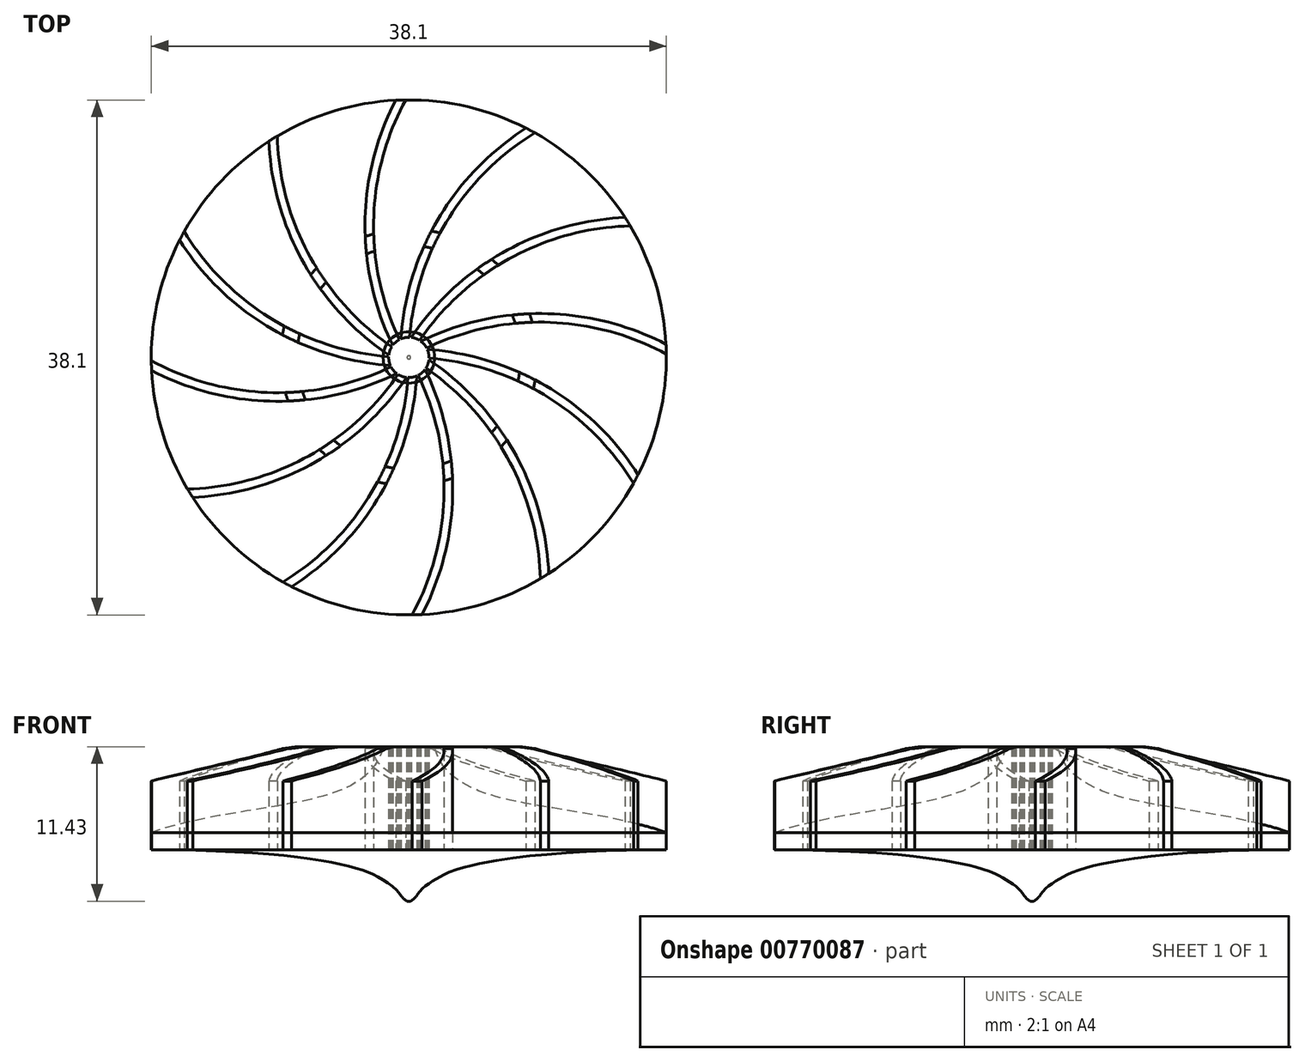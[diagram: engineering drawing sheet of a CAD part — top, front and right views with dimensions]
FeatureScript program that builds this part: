
annotation { "Feature Type Name" : "Feature", "Feature Type Description" : "" }
export const myFeature = defineFeature(function(context is Context, id is Id, definition is map)
    precondition{}
    {
        {
            var Q0;
            Q0=qCreatedBy(makeId("Top.planeOp"),FACE);
            var sketch = newSketch(context, id + "F0", { "sketchPlane" : qUnion([Q0])});
            skCircle(sketch, "E0", {"center": v(0, 0) * mm, "radius": 19.05 * mm});
            skPoint(sketch, "E1", {"position": v(-0.24, 19.05) * mm});
            skPoint(sketch, "E2.1.0", {"position": v(-9.73, 16.38) * mm});
            skPoint(sketch, "E2.2.0", {"position": v(-16.62, 9.32) * mm});
            skPoint(sketch, "E3.0.3.0", {"position": v(-19.05, -0.24) * mm});
            skPoint(sketch, "E3.0.4.0", {"position": v(-16.38, -9.73) * mm});
            skPoint(sketch, "E3.0.5.0", {"position": v(-9.32, -16.62) * mm});
            skPoint(sketch, "E3.0.6.0", {"position": v(0.24, -19.05) * mm});
            skPoint(sketch, "E3.0.7.0", {"position": v(9.73, -16.38) * mm});
            skPoint(sketch, "E3.0.8.0", {"position": v(16.62, -9.32) * mm});
            skPoint(sketch, "E3.0.9.0", {"position": v(19.05, 0.24) * mm});
            skPoint(sketch, "E3.0.10.0", {"position": v(16.38, 9.73) * mm});
            skPoint(sketch, "E3.0.11.0", {"position": v(9.32, 16.62) * mm});
            skArc(sketch, "E4", {"start": v(9.32, 16.62) * mm, "mid": v(2.49, 9.53) * mm, "end": v(0, 0) * mm});
            skArc(sketch, "E5.0", {"start": v(8.67, 16.96) * mm, "mid": v(1.84, 9.67) * mm, "end": v(-0.63, 0) * mm});
            skArc(sketch, "E6.1.0", {"start": v(-0.24, 19.05) * mm, "mid": v(-2.6, 9.5) * mm, "end": v(0, 0) * mm});
            skArc(sketch, "E6.1.1", {"start": v(-0.97, 19.03) * mm, "mid": v(-3.24, 9.3) * mm, "end": v(-0.55, -0.32) * mm});
            skArc(sketch, "E6.2.0", {"start": v(-9.73, 16.38) * mm, "mid": v(-7, 6.92) * mm, "end": v(0, 0) * mm});
            skArc(sketch, "E6.2.1", {"start": v(-10.35, 16) * mm, "mid": v(-7.46, 6.43) * mm, "end": v(-0.32, -0.55) * mm});
            skArc(sketch, "E6.3.0", {"start": v(-16.62, 9.32) * mm, "mid": v(-9.53, 2.49) * mm, "end": v(0, 0) * mm});
            skArc(sketch, "E6.3.1", {"start": v(-16.96, 8.67) * mm, "mid": v(-9.67, 1.84) * mm, "end": v(0, -0.63) * mm});
            skArc(sketch, "E6.4.0", {"start": v(-19.05, -0.24) * mm, "mid": v(-9.5, -2.6) * mm, "end": v(0, 0) * mm});
            skArc(sketch, "E6.4.1", {"start": v(-19.03, -0.97) * mm, "mid": v(-9.3, -3.24) * mm, "end": v(0.32, -0.55) * mm});
            skArc(sketch, "E6.5.0", {"start": v(-16.38, -9.73) * mm, "mid": v(-6.92, -7) * mm, "end": v(0, 0) * mm});
            skArc(sketch, "E6.5.1", {"start": v(-16, -10.35) * mm, "mid": v(-6.43, -7.46) * mm, "end": v(0.55, -0.32) * mm});
            skArc(sketch, "E6.6.0", {"start": v(-9.32, -16.62) * mm, "mid": v(-2.49, -9.53) * mm, "end": v(0, 0) * mm});
            skArc(sketch, "E6.6.1", {"start": v(-8.67, -16.96) * mm, "mid": v(-1.84, -9.67) * mm, "end": v(0.63, 0) * mm});
            skArc(sketch, "E6.7.0", {"start": v(0.24, -19.05) * mm, "mid": v(2.6, -9.5) * mm, "end": v(0, 0) * mm});
            skArc(sketch, "E6.7.1", {"start": v(0.97, -19.03) * mm, "mid": v(3.24, -9.3) * mm, "end": v(0.55, 0.32) * mm});
            skArc(sketch, "E6.8.0", {"start": v(9.73, -16.38) * mm, "mid": v(7, -6.92) * mm, "end": v(0, 0) * mm});
            skArc(sketch, "E6.8.1", {"start": v(10.35, -16) * mm, "mid": v(7.46, -6.43) * mm, "end": v(0.32, 0.55) * mm});
            skArc(sketch, "E6.9.0", {"start": v(16.62, -9.32) * mm, "mid": v(9.53, -2.49) * mm, "end": v(0, 0) * mm});
            skArc(sketch, "E6.9.1", {"start": v(16.96, -8.67) * mm, "mid": v(9.67, -1.84) * mm, "end": v(0, 0.63) * mm});
            skArc(sketch, "E6.10.0", {"start": v(19.05, 0.24) * mm, "mid": v(9.5, 2.6) * mm, "end": v(0, 0) * mm});
            skArc(sketch, "E6.10.1", {"start": v(19.03, 0.97) * mm, "mid": v(9.3, 3.24) * mm, "end": v(-0.32, 0.55) * mm});
            skArc(sketch, "E6.11.0", {"start": v(16.38, 9.73) * mm, "mid": v(6.92, 7) * mm, "end": v(0, 0) * mm});
            skArc(sketch, "E6.11.1", {"start": v(16, 10.35) * mm, "mid": v(6.43, 7.46) * mm, "end": v(-0.55, 0.32) * mm});
            skCircle(sketch, "E7", {"center": v(0, 0) * mm, "radius": 1.5 * mm});
            skSolve(sketch);
        }
        {
            var Q0;
            Q0=qCreatedBy(makeId("Top.planeOp"),FACE);
            var sketch = newSketch(context, id + "F1", { "sketchPlane" : qUnion([Q0])});
            skCircle(sketch, "E8", {"center": v(0, 0) * mm, "radius": 19.05 * mm});
            skSolve(sketch);
        }
        {
            var Q0;
            Q0 = qSketchRegion(id + "F1", true);
            extrude(context, id + "F2", {"entities" : qUnion([Q0]), "depth" : 6.35 * mm, "offsetDistance" : 25.4 * mm, "hasSecondDirection" : true, "secondDirectionOppositeDirection" : true, "secondDirectionDepth" : 1.27 * mm});
        }
        {
            var Q0;
            Q0=qCreatedBy(makeId("Front.planeOp"),FACE);
            var sketch = newSketch(context, id + "F3", { "sketchPlane" : qUnion([Q0])});
            skLineSegment(sketch, "E9.bottom", {"start": v(19.05, 6.35) * mm, "end": v(-19.05, 6.35) * mm});
            skLineSegment(sketch, "E9.left", {"start": v(19.05, 6.35) * mm, "end": v(19.05, -5.08) * mm});
            skLineSegment(sketch, "E9.right", {"start": v(-19.05, 6.35) * mm, "end": v(-19.05, -5.08) * mm});
            skPoint(sketch, "E9.middle", {"position": v(0, 0) * mm});
            skLineSegment(sketch, "E10", {"start": v(-19.05, -5.08) * mm, "end": v(19.05, -5.08) * mm});
            skLineSegment(sketch, "E11", {"start": v(-19.05, 0) * mm, "end": v(19.05, 0) * mm, "construction": true});
            skLineSegment(sketch, "E12", {"start": v(0, -5.08) * mm, "end": v(0, 6.35) * mm, "construction": true});
            skPoint(sketch, "E13", {"position": v(1.9, 6.35) * mm});
            skPoint(sketch, "E14", {"position": v(19.05, 1.27) * mm});
            skFitSpline(sketch, "E15", {"points": [v(1.9, 6.35) * mm, v(5.08, 3.11) * mm, v(19.05, 0) * mm, v(28.85, -6.98) * mm], "startDerivative": vector(3.87, -17.8) * mm, "endDerivative": vector(21.57, -22.67) * mm});
            skLineSegment(sketch, "E16", {"start": v(1.9, 6.35) * mm, "end": v(19.05, 6.35) * mm});
            skFitSpline(sketch, "E17", {"points": [v(19.05, -1.28) * mm, v(4.25, -2.54) * mm, v(2.03, -3.42) * mm, v(0.5, -4.83) * mm], "startDerivative": vector(-41.63, 0) * mm, "endDerivative": vector(-3.76, -8.36) * mm});
            skArc(sketch, "E18", {"start": v(0.13, -5.08) * mm, "mid": v(0.4, -4.87) * mm, "end": v(0.64, -4.6) * mm});
            skLineSegment(sketch, "E19", {"start": v(0, -5.08) * mm, "end": v(0, -1.28) * mm});
            skLineSegment(sketch, "E20", {"start": v(0, -1.28) * mm, "end": v(19.05, -1.28) * mm});
            skSolve(sketch);
        }
        {
            var Q0;
            {var subQ0=sQuery(id+"F3.wireOp",EDGE,"E15");Q0=makeQuery(id+"F3.imprint","IMPRINT",FACE,{"disambiguationData":[TD([[makeQuery(id+"F3.imprint","IMPRINT",EDGE,{"derivedFrom":subQ0}),1.0]])]});}
            var Q1;
            Q1=sQuery(id+"F3.wireOp",EDGE,"E12");
            revolve(context, id + "F4", {"operationType" : NewBodyOperationType.REMOVE, "surfaceOperationType" : NewSurfaceOperationType.NEW, "entities" : qUnion([Q0]), "axis" : qUnion([Q1]), "revolveType" : RevolveType.FULL});
        }
        {
            var Q0;
            {var subQ0=sQuery(id+"F0.wireOp",EDGE,"E6.4.0");var subQ1=sQuery(id+"F0.wireOp",EDGE,"E0");var subQ2=makeQuery(id+"F0.imprint","INTERSECT",VERTEX,{"derivedFrom":[subQ1,subQ0]});Q0=makeQuery(id+"F0.imprint","IMPRINT",FACE,{"disambiguationData":[TD([[makeQuery(id+"F0.imprint","IMPRINT",EDGE,{"disambiguationData":[TD([[subQ2,-1.0]])],"derivedFrom":subQ1}),1.0]])]});}
            var Q1;
            {var subQ0=sQuery(id+"F0.wireOp",EDGE,"E6.9.0");var subQ1=sQuery(id+"F0.wireOp",EDGE,"E0");var subQ2=makeQuery(id+"F0.imprint","INTERSECT",VERTEX,{"derivedFrom":[subQ1,subQ0]});Q1=makeQuery(id+"F0.imprint","IMPRINT",FACE,{"disambiguationData":[TD([[makeQuery(id+"F0.imprint","IMPRINT",EDGE,{"disambiguationData":[TD([[subQ2,-1.0]])],"derivedFrom":subQ1}),1.0]])]});}
            var Q2;
            {var subQ0=sQuery(id+"F0.wireOp",EDGE,"E6.6.0");var subQ1=sQuery(id+"F0.wireOp",EDGE,"E0");var subQ2=makeQuery(id+"F0.imprint","INTERSECT",VERTEX,{"derivedFrom":[subQ1,subQ0]});Q2=makeQuery(id+"F0.imprint","IMPRINT",FACE,{"disambiguationData":[TD([[makeQuery(id+"F0.imprint","IMPRINT",EDGE,{"disambiguationData":[TD([[subQ2,-1.0]])],"derivedFrom":subQ1}),1.0]])]});}
            var Q3;
            {var subQ0=sQuery(id+"F0.wireOp",EDGE,"E6.10.0");var subQ1=sQuery(id+"F0.wireOp",EDGE,"E0");var subQ2=makeQuery(id+"F0.imprint","INTERSECT",VERTEX,{"derivedFrom":[subQ1,subQ0]});Q3=makeQuery(id+"F0.imprint","IMPRINT",FACE,{"disambiguationData":[TD([[makeQuery(id+"F0.imprint","IMPRINT",EDGE,{"disambiguationData":[TD([[subQ2,-1.0]])],"derivedFrom":subQ1}),1.0]])]});}
            var Q4;
            {var subQ0=sQuery(id+"F0.wireOp",EDGE,"E6.3.0");var subQ1=sQuery(id+"F0.wireOp",EDGE,"E0");var subQ2=makeQuery(id+"F0.imprint","INTERSECT",VERTEX,{"derivedFrom":[subQ1,subQ0]});Q4=makeQuery(id+"F0.imprint","IMPRINT",FACE,{"disambiguationData":[TD([[makeQuery(id+"F0.imprint","IMPRINT",EDGE,{"disambiguationData":[TD([[subQ2,-1.0]])],"derivedFrom":subQ1}),1.0]])]});}
            var Q5;
            {var subQ0=sQuery(id+"F0.wireOp",EDGE,"E6.8.0");var subQ1=sQuery(id+"F0.wireOp",EDGE,"E0");var subQ2=makeQuery(id+"F0.imprint","INTERSECT",VERTEX,{"derivedFrom":[subQ1,subQ0]});Q5=makeQuery(id+"F0.imprint","IMPRINT",FACE,{"disambiguationData":[TD([[makeQuery(id+"F0.imprint","IMPRINT",EDGE,{"disambiguationData":[TD([[subQ2,-1.0]])],"derivedFrom":subQ1}),1.0]])]});}
            var Q6;
            {var subQ0=sQuery(id+"F0.wireOp",EDGE,"E6.7.0");var subQ1=sQuery(id+"F0.wireOp",EDGE,"E0");var subQ2=makeQuery(id+"F0.imprint","INTERSECT",VERTEX,{"derivedFrom":[subQ1,subQ0]});Q6=makeQuery(id+"F0.imprint","IMPRINT",FACE,{"disambiguationData":[TD([[makeQuery(id+"F0.imprint","IMPRINT",EDGE,{"disambiguationData":[TD([[subQ2,-1.0]])],"derivedFrom":subQ1}),1.0]])]});}
            var Q7;
            {var subQ0=sQuery(id+"F0.wireOp",EDGE,"E6.11.0");var subQ1=sQuery(id+"F0.wireOp",EDGE,"E0");var subQ2=makeQuery(id+"F0.imprint","INTERSECT",VERTEX,{"derivedFrom":[subQ1,subQ0]});Q7=makeQuery(id+"F0.imprint","IMPRINT",FACE,{"disambiguationData":[TD([[makeQuery(id+"F0.imprint","IMPRINT",EDGE,{"disambiguationData":[TD([[subQ2,-1.0]])],"derivedFrom":subQ1}),1.0]])]});}
            var Q8;
            {var subQ0=sQuery(id+"F0.wireOp",EDGE,"E6.1.0");var subQ1=sQuery(id+"F0.wireOp",EDGE,"E0");var subQ2=makeQuery(id+"F0.imprint","INTERSECT",VERTEX,{"derivedFrom":[subQ1,subQ0]});Q8=makeQuery(id+"F0.imprint","IMPRINT",FACE,{"disambiguationData":[TD([[makeQuery(id+"F0.imprint","IMPRINT",EDGE,{"disambiguationData":[TD([[subQ2,-1.0]])],"derivedFrom":subQ1}),1.0]])]});}
            var Q9;
            {var subQ0=sQuery(id+"F0.wireOp",EDGE,"E6.5.0");var subQ1=sQuery(id+"F0.wireOp",EDGE,"E0");var subQ2=makeQuery(id+"F0.imprint","INTERSECT",VERTEX,{"derivedFrom":[subQ1,subQ0]});Q9=makeQuery(id+"F0.imprint","IMPRINT",FACE,{"disambiguationData":[TD([[makeQuery(id+"F0.imprint","IMPRINT",EDGE,{"disambiguationData":[TD([[subQ2,-1.0]])],"derivedFrom":subQ1}),1.0]])]});}
            var Q10;
            {var subQ0=sQuery(id+"F0.wireOp",EDGE,"E4");var subQ1=sQuery(id+"F0.wireOp",EDGE,"E0");var subQ2=makeQuery(id+"F0.imprint","INTERSECT",VERTEX,{"derivedFrom":[subQ1,subQ0]});Q10=makeQuery(id+"F0.imprint","IMPRINT",FACE,{"disambiguationData":[TD([[makeQuery(id+"F0.imprint","IMPRINT",EDGE,{"disambiguationData":[TD([[subQ2,-1.0]])],"derivedFrom":subQ1}),1.0]])]});}
            var Q11;
            {var subQ0=sQuery(id+"F0.wireOp",EDGE,"E6.2.0");var subQ1=sQuery(id+"F0.wireOp",EDGE,"E0");var subQ2=makeQuery(id+"F0.imprint","INTERSECT",VERTEX,{"derivedFrom":[subQ1,subQ0]});Q11=makeQuery(id+"F0.imprint","IMPRINT",FACE,{"disambiguationData":[TD([[makeQuery(id+"F0.imprint","IMPRINT",EDGE,{"disambiguationData":[TD([[subQ2,-1.0]])],"derivedFrom":subQ1}),1.0]])]});}
            extrude(context, id + "F5", {"entities" : qUnion([Q0, Q1, Q2, Q3, Q4, Q5, Q6, Q7, Q8, Q9, Q10, Q11]), "depth" : 6.35 * mm, "offsetDistance" : 25.4 * mm, "hasSecondDirection" : true, "secondDirectionOppositeDirection" : true, "secondDirectionDepth" : 1.27 * mm});
        }
        {
            var Q0;
            {var subQ0=sQuery(id+"F0.wireOp",EDGE,"E0");Q0=makeQuery(id+"F5.opExtrude","CAP_EDGE",EDGE,{"disambiguationData":[OSD([subQ0]),TDD([makeQuery(id+"F0.imprint","IMPRINT",EDGE,{"disambiguationData":[TD([[makeQuery(id+"F0.imprint","INTERSECT",VERTEX,{"derivedFrom":[subQ0,sQuery(id+"F0.wireOp",EDGE,"E6.8.0")]}),-1.0]])],"derivedFrom":subQ0})])],"isStart":false});}
            var Q1;
            {var subQ0=sQuery(id+"F0.wireOp",EDGE,"E0");Q1=makeQuery(id+"F5.opExtrude","CAP_EDGE",EDGE,{"disambiguationData":[OSD([subQ0]),TDD([makeQuery(id+"F0.imprint","IMPRINT",EDGE,{"disambiguationData":[TD([[makeQuery(id+"F0.imprint","INTERSECT",VERTEX,{"derivedFrom":[subQ0,sQuery(id+"F0.wireOp",EDGE,"E6.7.0")]}),-1.0]])],"derivedFrom":subQ0})])],"isStart":false});}
            var Q2;
            {var subQ0=sQuery(id+"F0.wireOp",EDGE,"E0");Q2=makeQuery(id+"F5.opExtrude","CAP_EDGE",EDGE,{"disambiguationData":[OSD([subQ0]),TDD([makeQuery(id+"F0.imprint","IMPRINT",EDGE,{"disambiguationData":[TD([[makeQuery(id+"F0.imprint","INTERSECT",VERTEX,{"derivedFrom":[subQ0,sQuery(id+"F0.wireOp",EDGE,"E6.6.0")]}),-1.0]])],"derivedFrom":subQ0})])],"isStart":false});}
            var Q3;
            {var subQ0=sQuery(id+"F0.wireOp",EDGE,"E0");Q3=makeQuery(id+"F5.opExtrude","CAP_EDGE",EDGE,{"disambiguationData":[OSD([subQ0]),TDD([makeQuery(id+"F0.imprint","IMPRINT",EDGE,{"disambiguationData":[TD([[makeQuery(id+"F0.imprint","INTERSECT",VERTEX,{"derivedFrom":[subQ0,sQuery(id+"F0.wireOp",EDGE,"E6.5.0")]}),-1.0]])],"derivedFrom":subQ0})])],"isStart":false});}
            var Q4;
            {var subQ0=sQuery(id+"F0.wireOp",EDGE,"E0");Q4=makeQuery(id+"F5.opExtrude","CAP_EDGE",EDGE,{"disambiguationData":[OSD([subQ0]),TDD([makeQuery(id+"F0.imprint","IMPRINT",EDGE,{"disambiguationData":[TD([[makeQuery(id+"F0.imprint","INTERSECT",VERTEX,{"derivedFrom":[subQ0,sQuery(id+"F0.wireOp",EDGE,"E6.4.0")]}),-1.0]])],"derivedFrom":subQ0})])],"isStart":false});}
            var Q5;
            {var subQ0=sQuery(id+"F0.wireOp",EDGE,"E0");Q5=makeQuery(id+"F5.opExtrude","CAP_EDGE",EDGE,{"disambiguationData":[OSD([subQ0]),TDD([makeQuery(id+"F0.imprint","IMPRINT",EDGE,{"disambiguationData":[TD([[makeQuery(id+"F0.imprint","INTERSECT",VERTEX,{"derivedFrom":[subQ0,sQuery(id+"F0.wireOp",EDGE,"E6.3.0")]}),-1.0]])],"derivedFrom":subQ0})])],"isStart":false});}
            var Q6;
            {var subQ0=sQuery(id+"F0.wireOp",EDGE,"E0");Q6=makeQuery(id+"F5.opExtrude","CAP_EDGE",EDGE,{"disambiguationData":[OSD([subQ0]),TDD([makeQuery(id+"F0.imprint","IMPRINT",EDGE,{"disambiguationData":[TD([[makeQuery(id+"F0.imprint","INTERSECT",VERTEX,{"derivedFrom":[subQ0,sQuery(id+"F0.wireOp",EDGE,"E6.2.0")]}),-1.0]])],"derivedFrom":subQ0})])],"isStart":false});}
            var Q7;
            {var subQ0=sQuery(id+"F0.wireOp",EDGE,"E0");Q7=makeQuery(id+"F5.opExtrude","CAP_EDGE",EDGE,{"disambiguationData":[OSD([subQ0]),TDD([makeQuery(id+"F0.imprint","IMPRINT",EDGE,{"disambiguationData":[TD([[makeQuery(id+"F0.imprint","INTERSECT",VERTEX,{"derivedFrom":[subQ0,sQuery(id+"F0.wireOp",EDGE,"E6.1.0")]}),-1.0]])],"derivedFrom":subQ0})])],"isStart":false});}
            var Q8;
            {var subQ0=sQuery(id+"F0.wireOp",EDGE,"E0");Q8=makeQuery(id+"F5.opExtrude","CAP_EDGE",EDGE,{"disambiguationData":[OSD([subQ0]),TDD([makeQuery(id+"F0.imprint","IMPRINT",EDGE,{"disambiguationData":[TD([[makeQuery(id+"F0.imprint","INTERSECT",VERTEX,{"derivedFrom":[subQ0,sQuery(id+"F0.wireOp",EDGE,"E4")]}),-1.0]])],"derivedFrom":subQ0})])],"isStart":false});}
            var Q9;
            {var subQ0=sQuery(id+"F0.wireOp",EDGE,"E0");Q9=makeQuery(id+"F5.opExtrude","CAP_EDGE",EDGE,{"disambiguationData":[OSD([subQ0]),TDD([makeQuery(id+"F0.imprint","IMPRINT",EDGE,{"disambiguationData":[TD([[makeQuery(id+"F0.imprint","INTERSECT",VERTEX,{"derivedFrom":[subQ0,sQuery(id+"F0.wireOp",EDGE,"E6.11.0")]}),-1.0]])],"derivedFrom":subQ0})])],"isStart":false});}
            var Q10;
            {var subQ0=sQuery(id+"F0.wireOp",EDGE,"E0");Q10=makeQuery(id+"F5.opExtrude","CAP_EDGE",EDGE,{"disambiguationData":[OSD([subQ0]),TDD([makeQuery(id+"F0.imprint","IMPRINT",EDGE,{"disambiguationData":[TD([[makeQuery(id+"F0.imprint","INTERSECT",VERTEX,{"derivedFrom":[subQ0,sQuery(id+"F0.wireOp",EDGE,"E6.10.0")]}),-1.0]])],"derivedFrom":subQ0})])],"isStart":false});}
            var Q11;
            {var subQ0=sQuery(id+"F0.wireOp",EDGE,"E0");Q11=makeQuery(id+"F5.opExtrude","CAP_EDGE",EDGE,{"disambiguationData":[OSD([subQ0]),TDD([makeQuery(id+"F0.imprint","IMPRINT",EDGE,{"disambiguationData":[TD([[makeQuery(id+"F0.imprint","INTERSECT",VERTEX,{"derivedFrom":[subQ0,sQuery(id+"F0.wireOp",EDGE,"E6.9.0")]}),-1.0]])],"derivedFrom":subQ0})])],"isStart":false});}
            chamfer(context, id + "F6", {"entities" : qUnion([Q0, Q1, Q2, Q3, Q4, Q5, Q6, Q7, Q8, Q9, Q10, Q11]), "chamferType" : ChamferType.TWO_OFFSETS, "width1" : 10.16 * mm, "oppositeDirection" : false, "width2" : 2.54 * mm, "tangentPropagation" : true});
        }
        {
            var Q0;
            {var subQ0=sQuery(id+"F0.wireOp",EDGE,"E6.8.1");var subQ1=sQuery(id+"F0.wireOp",EDGE,"E6.8.0");var subQ2=sQuery(id+"F0.wireOp",EDGE,"E0");Q0=makeQuery(id+"F6.opChamfer","BLEND_EDGE",EDGE,{"blendedFrom":[makeQuery(id+"F5.opExtrude","CAP_EDGE",EDGE,{"disambiguationData":[OSD([subQ2]),TDD([makeQuery(id+"F0.imprint","IMPRINT",EDGE,{"disambiguationData":[TD([[makeQuery(id+"F0.imprint","INTERSECT",VERTEX,{"derivedFrom":[subQ2,subQ1]}),-1.0]])],"derivedFrom":subQ2})])],"isStart":false}),makeQuery(id+"F5.opExtrude","CAP_FACE",FACE,{"disambiguationData":[OSD([subQ2,subQ1,subQ0,sQuery(id+"F0.wireOp",EDGE,"E7")])],"isStart":false})],"blendedInto":[makeQuery(id+"F5.opExtrude","CAP_FACE",FACE,{"disambiguationData":[OSD([subQ2,subQ1,subQ0,sQuery(id+"F0.wireOp",EDGE,"E7")])],"isStart":false})]});}
            var Q1;
            {var subQ0=sQuery(id+"F0.wireOp",EDGE,"E6.7.1");var subQ1=sQuery(id+"F0.wireOp",EDGE,"E6.7.0");var subQ2=sQuery(id+"F0.wireOp",EDGE,"E0");Q1=makeQuery(id+"F6.opChamfer","BLEND_EDGE",EDGE,{"blendedFrom":[makeQuery(id+"F5.opExtrude","CAP_EDGE",EDGE,{"disambiguationData":[OSD([subQ2]),TDD([makeQuery(id+"F0.imprint","IMPRINT",EDGE,{"disambiguationData":[TD([[makeQuery(id+"F0.imprint","INTERSECT",VERTEX,{"derivedFrom":[subQ2,subQ1]}),-1.0]])],"derivedFrom":subQ2})])],"isStart":false}),makeQuery(id+"F5.opExtrude","CAP_FACE",FACE,{"disambiguationData":[OSD([subQ2,subQ1,subQ0,sQuery(id+"F0.wireOp",EDGE,"E7")])],"isStart":false})],"blendedInto":[makeQuery(id+"F5.opExtrude","CAP_FACE",FACE,{"disambiguationData":[OSD([subQ2,subQ1,subQ0,sQuery(id+"F0.wireOp",EDGE,"E7")])],"isStart":false})]});}
            var Q2;
            {var subQ0=sQuery(id+"F0.wireOp",EDGE,"E6.9.1");var subQ1=sQuery(id+"F0.wireOp",EDGE,"E6.9.0");var subQ2=sQuery(id+"F0.wireOp",EDGE,"E0");Q2=makeQuery(id+"F6.opChamfer","BLEND_EDGE",EDGE,{"blendedFrom":[makeQuery(id+"F5.opExtrude","CAP_EDGE",EDGE,{"disambiguationData":[OSD([subQ2]),TDD([makeQuery(id+"F0.imprint","IMPRINT",EDGE,{"disambiguationData":[TD([[makeQuery(id+"F0.imprint","INTERSECT",VERTEX,{"derivedFrom":[subQ2,subQ1]}),-1.0]])],"derivedFrom":subQ2})])],"isStart":false}),makeQuery(id+"F5.opExtrude","CAP_FACE",FACE,{"disambiguationData":[OSD([subQ2,subQ1,subQ0,sQuery(id+"F0.wireOp",EDGE,"E7")])],"isStart":false})],"blendedInto":[makeQuery(id+"F5.opExtrude","CAP_FACE",FACE,{"disambiguationData":[OSD([subQ2,subQ1,subQ0,sQuery(id+"F0.wireOp",EDGE,"E7")])],"isStart":false})]});}
            var Q3;
            {var subQ0=sQuery(id+"F0.wireOp",EDGE,"E6.10.1");var subQ1=sQuery(id+"F0.wireOp",EDGE,"E6.10.0");var subQ2=sQuery(id+"F0.wireOp",EDGE,"E0");Q3=makeQuery(id+"F6.opChamfer","BLEND_EDGE",EDGE,{"blendedFrom":[makeQuery(id+"F5.opExtrude","CAP_EDGE",EDGE,{"disambiguationData":[OSD([subQ2]),TDD([makeQuery(id+"F0.imprint","IMPRINT",EDGE,{"disambiguationData":[TD([[makeQuery(id+"F0.imprint","INTERSECT",VERTEX,{"derivedFrom":[subQ2,subQ1]}),-1.0]])],"derivedFrom":subQ2})])],"isStart":false}),makeQuery(id+"F5.opExtrude","CAP_FACE",FACE,{"disambiguationData":[OSD([subQ2,subQ1,subQ0,sQuery(id+"F0.wireOp",EDGE,"E7")])],"isStart":false})],"blendedInto":[makeQuery(id+"F5.opExtrude","CAP_FACE",FACE,{"disambiguationData":[OSD([subQ2,subQ1,subQ0,sQuery(id+"F0.wireOp",EDGE,"E7")])],"isStart":false})]});}
            var Q4;
            {var subQ0=sQuery(id+"F0.wireOp",EDGE,"E6.11.1");var subQ1=sQuery(id+"F0.wireOp",EDGE,"E6.11.0");var subQ2=sQuery(id+"F0.wireOp",EDGE,"E0");Q4=makeQuery(id+"F6.opChamfer","BLEND_EDGE",EDGE,{"blendedFrom":[makeQuery(id+"F5.opExtrude","CAP_EDGE",EDGE,{"disambiguationData":[OSD([subQ2]),TDD([makeQuery(id+"F0.imprint","IMPRINT",EDGE,{"disambiguationData":[TD([[makeQuery(id+"F0.imprint","INTERSECT",VERTEX,{"derivedFrom":[subQ2,subQ1]}),-1.0]])],"derivedFrom":subQ2})])],"isStart":false}),makeQuery(id+"F5.opExtrude","CAP_FACE",FACE,{"disambiguationData":[OSD([subQ2,subQ1,subQ0,sQuery(id+"F0.wireOp",EDGE,"E7")])],"isStart":false})],"blendedInto":[makeQuery(id+"F5.opExtrude","CAP_FACE",FACE,{"disambiguationData":[OSD([subQ2,subQ1,subQ0,sQuery(id+"F0.wireOp",EDGE,"E7")])],"isStart":false})]});}
            var Q5;
            {var subQ0=sQuery(id+"F0.wireOp",EDGE,"E5.0");var subQ1=sQuery(id+"F0.wireOp",EDGE,"E4");var subQ2=sQuery(id+"F0.wireOp",EDGE,"E0");Q5=makeQuery(id+"F6.opChamfer","BLEND_EDGE",EDGE,{"blendedFrom":[makeQuery(id+"F5.opExtrude","CAP_EDGE",EDGE,{"disambiguationData":[OSD([subQ2]),TDD([makeQuery(id+"F0.imprint","IMPRINT",EDGE,{"disambiguationData":[TD([[makeQuery(id+"F0.imprint","INTERSECT",VERTEX,{"derivedFrom":[subQ2,subQ1]}),-1.0]])],"derivedFrom":subQ2})])],"isStart":false}),makeQuery(id+"F5.opExtrude","CAP_FACE",FACE,{"disambiguationData":[OSD([subQ2,subQ1,subQ0,sQuery(id+"F0.wireOp",EDGE,"E7")])],"isStart":false})],"blendedInto":[makeQuery(id+"F5.opExtrude","CAP_FACE",FACE,{"disambiguationData":[OSD([subQ2,subQ1,subQ0,sQuery(id+"F0.wireOp",EDGE,"E7")])],"isStart":false})]});}
            var Q6;
            {var subQ0=sQuery(id+"F0.wireOp",EDGE,"E6.1.1");var subQ1=sQuery(id+"F0.wireOp",EDGE,"E6.1.0");var subQ2=sQuery(id+"F0.wireOp",EDGE,"E0");Q6=makeQuery(id+"F6.opChamfer","BLEND_EDGE",EDGE,{"blendedFrom":[makeQuery(id+"F5.opExtrude","CAP_EDGE",EDGE,{"disambiguationData":[OSD([subQ2]),TDD([makeQuery(id+"F0.imprint","IMPRINT",EDGE,{"disambiguationData":[TD([[makeQuery(id+"F0.imprint","INTERSECT",VERTEX,{"derivedFrom":[subQ2,subQ1]}),-1.0]])],"derivedFrom":subQ2})])],"isStart":false}),makeQuery(id+"F5.opExtrude","CAP_FACE",FACE,{"disambiguationData":[OSD([subQ2,subQ1,subQ0,sQuery(id+"F0.wireOp",EDGE,"E7")])],"isStart":false})],"blendedInto":[makeQuery(id+"F5.opExtrude","CAP_FACE",FACE,{"disambiguationData":[OSD([subQ2,subQ1,subQ0,sQuery(id+"F0.wireOp",EDGE,"E7")])],"isStart":false})]});}
            var Q7;
            {var subQ0=sQuery(id+"F0.wireOp",EDGE,"E6.2.1");var subQ1=sQuery(id+"F0.wireOp",EDGE,"E6.2.0");var subQ2=sQuery(id+"F0.wireOp",EDGE,"E0");Q7=makeQuery(id+"F6.opChamfer","BLEND_EDGE",EDGE,{"blendedFrom":[makeQuery(id+"F5.opExtrude","CAP_EDGE",EDGE,{"disambiguationData":[OSD([subQ2]),TDD([makeQuery(id+"F0.imprint","IMPRINT",EDGE,{"disambiguationData":[TD([[makeQuery(id+"F0.imprint","INTERSECT",VERTEX,{"derivedFrom":[subQ2,subQ1]}),-1.0]])],"derivedFrom":subQ2})])],"isStart":false}),makeQuery(id+"F5.opExtrude","CAP_FACE",FACE,{"disambiguationData":[OSD([subQ2,subQ1,subQ0,sQuery(id+"F0.wireOp",EDGE,"E7")])],"isStart":false})],"blendedInto":[makeQuery(id+"F5.opExtrude","CAP_FACE",FACE,{"disambiguationData":[OSD([subQ2,subQ1,subQ0,sQuery(id+"F0.wireOp",EDGE,"E7")])],"isStart":false})]});}
            var Q8;
            {var subQ0=sQuery(id+"F0.wireOp",EDGE,"E6.3.1");var subQ1=sQuery(id+"F0.wireOp",EDGE,"E6.3.0");var subQ2=sQuery(id+"F0.wireOp",EDGE,"E0");Q8=makeQuery(id+"F6.opChamfer","BLEND_EDGE",EDGE,{"blendedFrom":[makeQuery(id+"F5.opExtrude","CAP_EDGE",EDGE,{"disambiguationData":[OSD([subQ2]),TDD([makeQuery(id+"F0.imprint","IMPRINT",EDGE,{"disambiguationData":[TD([[makeQuery(id+"F0.imprint","INTERSECT",VERTEX,{"derivedFrom":[subQ2,subQ1]}),-1.0]])],"derivedFrom":subQ2})])],"isStart":false}),makeQuery(id+"F5.opExtrude","CAP_FACE",FACE,{"disambiguationData":[OSD([subQ2,subQ1,subQ0,sQuery(id+"F0.wireOp",EDGE,"E7")])],"isStart":false})],"blendedInto":[makeQuery(id+"F5.opExtrude","CAP_FACE",FACE,{"disambiguationData":[OSD([subQ2,subQ1,subQ0,sQuery(id+"F0.wireOp",EDGE,"E7")])],"isStart":false})]});}
            var Q9;
            {var subQ0=sQuery(id+"F0.wireOp",EDGE,"E6.4.1");var subQ1=sQuery(id+"F0.wireOp",EDGE,"E6.4.0");var subQ2=sQuery(id+"F0.wireOp",EDGE,"E0");Q9=makeQuery(id+"F6.opChamfer","BLEND_EDGE",EDGE,{"blendedFrom":[makeQuery(id+"F5.opExtrude","CAP_EDGE",EDGE,{"disambiguationData":[OSD([subQ2]),TDD([makeQuery(id+"F0.imprint","IMPRINT",EDGE,{"disambiguationData":[TD([[makeQuery(id+"F0.imprint","INTERSECT",VERTEX,{"derivedFrom":[subQ2,subQ1]}),-1.0]])],"derivedFrom":subQ2})])],"isStart":false}),makeQuery(id+"F5.opExtrude","CAP_FACE",FACE,{"disambiguationData":[OSD([subQ2,subQ1,subQ0,sQuery(id+"F0.wireOp",EDGE,"E7")])],"isStart":false})],"blendedInto":[makeQuery(id+"F5.opExtrude","CAP_FACE",FACE,{"disambiguationData":[OSD([subQ2,subQ1,subQ0,sQuery(id+"F0.wireOp",EDGE,"E7")])],"isStart":false})]});}
            var Q10;
            {var subQ0=sQuery(id+"F0.wireOp",EDGE,"E6.6.1");var subQ1=sQuery(id+"F0.wireOp",EDGE,"E6.6.0");var subQ2=sQuery(id+"F0.wireOp",EDGE,"E0");Q10=makeQuery(id+"F6.opChamfer","BLEND_EDGE",EDGE,{"blendedFrom":[makeQuery(id+"F5.opExtrude","CAP_EDGE",EDGE,{"disambiguationData":[OSD([subQ2]),TDD([makeQuery(id+"F0.imprint","IMPRINT",EDGE,{"disambiguationData":[TD([[makeQuery(id+"F0.imprint","INTERSECT",VERTEX,{"derivedFrom":[subQ2,subQ1]}),-1.0]])],"derivedFrom":subQ2})])],"isStart":false}),makeQuery(id+"F5.opExtrude","CAP_FACE",FACE,{"disambiguationData":[OSD([subQ2,subQ1,subQ0,sQuery(id+"F0.wireOp",EDGE,"E7")])],"isStart":false})],"blendedInto":[makeQuery(id+"F5.opExtrude","CAP_FACE",FACE,{"disambiguationData":[OSD([subQ2,subQ1,subQ0,sQuery(id+"F0.wireOp",EDGE,"E7")])],"isStart":false})]});}
            var Q11;
            {var subQ0=sQuery(id+"F0.wireOp",EDGE,"E6.5.1");var subQ1=sQuery(id+"F0.wireOp",EDGE,"E6.5.0");var subQ2=sQuery(id+"F0.wireOp",EDGE,"E0");Q11=makeQuery(id+"F6.opChamfer","BLEND_EDGE",EDGE,{"blendedFrom":[makeQuery(id+"F5.opExtrude","CAP_EDGE",EDGE,{"disambiguationData":[OSD([subQ2]),TDD([makeQuery(id+"F0.imprint","IMPRINT",EDGE,{"disambiguationData":[TD([[makeQuery(id+"F0.imprint","INTERSECT",VERTEX,{"derivedFrom":[subQ2,subQ1]}),-1.0]])],"derivedFrom":subQ2})])],"isStart":false}),makeQuery(id+"F5.opExtrude","CAP_FACE",FACE,{"disambiguationData":[OSD([subQ2,subQ1,subQ0,sQuery(id+"F0.wireOp",EDGE,"E7")])],"isStart":false})],"blendedInto":[makeQuery(id+"F5.opExtrude","CAP_FACE",FACE,{"disambiguationData":[OSD([subQ2,subQ1,subQ0,sQuery(id+"F0.wireOp",EDGE,"E7")])],"isStart":false})]});}
            chamfer(context, id + "F7", {"entities" : qUnion([Q0, Q1, Q2, Q3, Q4, Q5, Q6, Q7, Q8, Q9, Q10, Q11]), "width" : 5.08 * mm, "tangentPropagation" : true});
        }
        {
            var Q0;
            {var subQ1=sQuery(id+"F3.wireOp",EDGE,"E9.right");Q0=makeQuery(id+"F3.imprint","IMPRINT",FACE,{"disambiguationData":[TD([[makeQuery(id+"F3.imprint","IMPRINT",EDGE,{"derivedFrom":subQ1}),1.0]])]});}
            var sketch = newSketch(context, id + "F8", { "sketchPlane" : qUnion([Q0])});
            skLineSegment(sketch, "E21.bottom", {"start": v(-19.05, -4.25) * mm, "end": v(19.05, -4.25) * mm});
            skLineSegment(sketch, "E21.top", {"start": v(-19.05, -1.27) * mm, "end": v(19.05, -1.27) * mm});
            skLineSegment(sketch, "E21.left", {"start": v(-19.05, -4.25) * mm, "end": v(-19.05, -1.27) * mm});
            skLineSegment(sketch, "E21.right", {"start": v(19.05, -4.25) * mm, "end": v(19.05, -1.27) * mm});
            skPoint(sketch, "E22", {"position": v(0, -4.25) * mm});
            skSolve(sketch);
        }
        {
            var Q0;
            {var subQ7=sQuery(id+"F8.wireOp",EDGE,"E21.top");Q0=makeQuery(id+"F8.imprint","IMPRINT",FACE,{"disambiguationData":[TD([[makeQuery(id+"F8.imprint","IMPRINT",EDGE,{"derivedFrom":subQ7}),-1.0]])]});}
            var Q1;
            {var subQ0=sQuery(id+"F8.wireOp",EDGE,"E21.right");var subQ1=sQuery(id+"F8.wireOp",EDGE,"E21.bottom");var subQ2=makeQuery(id+"F8.imprint","INTERSECT",VERTEX,{"derivedFrom":[subQ1,subQ0]});Q1=makeQuery(id+"F8.imprint","IMPRINT",FACE,{"disambiguationData":[TD([[makeQuery(id+"F8.imprint","IMPRINT",EDGE,{"disambiguationData":[TD([[subQ2,1.0]])],"derivedFrom":subQ1}),1.0]])]});}
            extrude(context, id + "F9", {"entities" : qUnion([Q0, Q1]), "operationType" : NewBodyOperationType.REMOVE, "endBound" : BoundingType.SYMMETRIC, "oppositeDirection" : true, "depth" : 127 * mm, "offsetDistance" : 25.4 * mm, "hasSecondDirection" : true, "secondDirectionBound" : SecondDirectionBoundingType.THROUGH_ALL, "secondDirectionOppositeDirection" : false, "secondDirectionDepth" : 25.4 * mm});
        }
        {
            var Q0;
            Q0=makeQuery(id+"F3.imprint","IMPRINT",FACE,{"disambiguationData":[TD([[makeQuery(id+"F3.imprint","IMPRINT",EDGE,{"derivedFrom":sQuery(id+"F3.wireOp",EDGE,"E17")}),-1.0]])]});
            var Q1;
            Q1=sQuery(id+"F3.wireOp",EDGE,"E12");
            revolve(context, id + "F10", {"surfaceOperationType" : NewSurfaceOperationType.NEW, "entities" : qUnion([Q0]), "axis" : qUnion([Q1]), "revolveType" : RevolveType.FULL});
        }
    });
